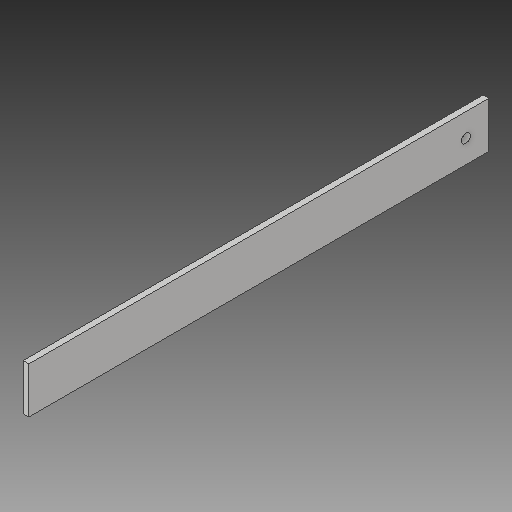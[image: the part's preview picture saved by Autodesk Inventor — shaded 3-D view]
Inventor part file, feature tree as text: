
AUTODESK INVENTOR PART (.ipt)
format: ipt  version: 2018 (Build 220112000, 112)  size: 97,280 bytes
history: native  units: in
note: dims shown in document units (in); Inventor stores cm internally (conversion verified against a paired STEP export)
features: extrude x1, hole x1, sketch x1
ambient origin geometry x8: Origin, YZ Plane, XZ Plane, XY Plane, X Axis, Y Axis, Z Axis, Center Point
bodies: Solid1 (feature_tree)
feature tree (3):
  extrude  "Extrusion1"  Depth=10.0in
  hole  "Hole1"  [1 undecoded]
  sketch  "Sketch1"  dims[d0=1.0in d1=10.0in d2=0.125in d3=0.0in d4=0.5in d5=0.5in d6=0.2031in d7=0.75in d8=0.375in d9=0.25in d10=0.5635in d11=1.0in d12=0.8108in]
note: 1 required parameter value undecoded (feature->parameter linkage not recoverable at this tier; creation-order binding heuristic only, values carry confidence <= 0.55)
